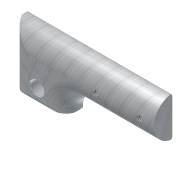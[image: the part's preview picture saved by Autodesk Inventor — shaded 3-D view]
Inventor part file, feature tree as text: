
AUTODESK INVENTOR PART (.ipt)
format: ipt  version: 2012 (Build 160160000, 160)  size: 212,480 bytes
history: native  units: in
note: dims shown in document units (in); Inventor stores cm internally (conversion verified against a paired STEP export)
features: sketch x6, extrude x4, projected_geometry x3, hole x2, sweep x2, fillet x1, pattern_linear x1
ambient origin geometry x8: Origin, YZ Plane, XZ Plane, XY Plane, X Axis, Y Axis, Z Axis, Center Point
bodies: Solid1 (feature_tree)
feature tree (19):
  extrude  "Extrusion1"  Depth=1.375in
  fillet  "Fillet1"  Radius=2.0in
  extrude  "Extrusion2"  Depth=0.75in TaperAngle=0.0deg
  hole  "Hole1"  [1 undecoded]
  pattern_linear  "Rectangular Pattern1"  Spacing1=0.6875in  [1 undecoded]
  hole  "Hole2"  [1 undecoded]
  extrude  "Extrusion3"  Depth=4.0in
  sketch  "Sketch4"  dims[d11=0.125in]
  sketch  "Sketch5"  dims[d12=8.0in]
  sweep  "Sweep1"
  sweep  "Sweep2"
  extrude  "Extrusion4"  Depth=0.0625in
  sketch  "Sketch1"  dims[d0=2.0in d1=1.375in d2=2.0in]
  sketch  "Sketch2"  dims[d3=5.0in d6=0.75in d7=0.0in]
  sketch  "Sketch3"  dims[d8=0.4375in d9=0.6875in]
  projected_geometry  "Projected Loop1"
  projected_geometry  "Projected Loop2"
  projected_geometry  "Projected Loop3"
  sketch  "Sketch6"  dims[d13=42.0in d14=0.0in d15=0.6875in d16=0.5in d17=0.196in d18=0.5in d19=0.375in d20=0.25in d21=0.5635in d22=0.75in d23=0.8108in d24=0.7874in d26=1.5in d27=4.0in d28=0.456in d29=0.5in d30=0.5in d31=0.375in d32=0.25in d33=0.5635in d34=0.75in d35=0.8108in d39=0.125in d40=20.0in d41=0.0in d42=0.0625in d43=0.0in d44=0.0in d45=0.25in d46=20.0in d47=0.0in]
note: 3 required parameter values undecoded (feature->parameter linkage not recoverable at this tier; creation-order binding heuristic only, values carry confidence <= 0.55)
